# Revit family: DR6015551_Dispensador Jabon
name_source: partatom
category: Furniture
units: mm (PartAtom-declared; Revit-internal decimal feet)

## family parameters
Always vertical = Yes
Cut with Voids When Loaded = No
Host = Wall
OmniClass Number = 23.31.25.29.11
OmniClass Title = Hand Soap Holders
Room Calculation Point = No
Shared = No

## types (1)
- Type 1
    Alto = 133 mm  [stored 0.436352 ft]
    Altura = 900 mm  [stored 2.95276 ft]
    Ancho = 86 mm  [stored 0.282152 ft]
    Creado por = IDD
    Description = Adquiere estos accesorios que reflejan las últimas tendencias de diseño y se conviernten en el mejor complemento para tu baño. ¡Todo lo que necitabas está aquí!
    Fecha de creación = 11/08/2020
    Garantía = 30 Años
    Garantía Acabados = 5 Años
    Manufacturer = Corona
    Material = Corona_Cromado
    Peso Bruto aprox = 4,8 kg. - 10,58 lb.
    Peso Neto aprox = 420 gr.
    Profundidad = 105 mm  [stored 0.344488 ft]
    Referencia = DR6015551
    Resistencia a cargas o peso máximo = 9 kg. (19,84 lb.)
    URL = https://corona.co

note: [stored X ft] marks values corroborated as IEEE doubles in the binary element streams (Revit-internal decimal feet)

## geometry (parser evidence)
native form markers: Sweep x8
no freeform markers — native parametric forms only
